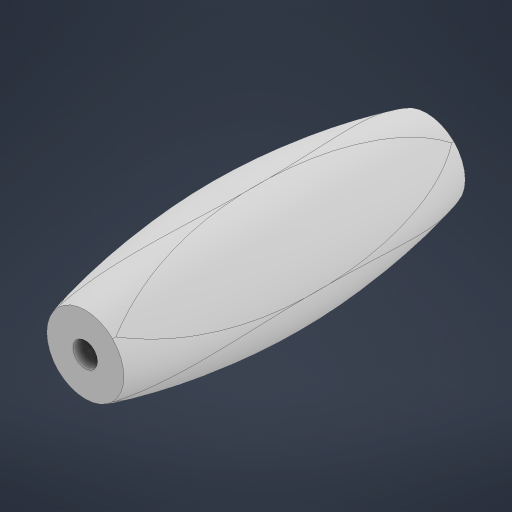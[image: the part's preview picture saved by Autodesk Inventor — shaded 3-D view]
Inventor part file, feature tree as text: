
AUTODESK INVENTOR PART (.ipt)
format: ipt  version: 2023 (Build 270158000, 158)  size: 424,448 bytes
history: native  units: mm
features: extrude x4, sketch x3, fillet x2
ambient origin geometry x8: Origin, YZ Plane, XZ Plane, XY Plane, X Axis, Y Axis, Z Axis, Center Point
bodies: Solid1 (feature_tree)
feature tree (9):
  extrude  "Extrusion1"  Depth=15.0mm
  sketch  "Sketch2"  dims[d2=3.0mm d3=41.999916mm d4=0.0mm]
  sketch  "Sketch3"  dims[d5=2.0mm d6=2.0mm d7=2.0mm d8=2.0mm d9=41.999916mm d10=0.0mm d11=41.999916mm d12=0.0mm d13=41.999916mm d14=0.0mm d15=7.49mm d16=5.0mm]
  extrude  "Extrusion2"  Depth=41.999916mm TaperAngle=0.0deg
  extrude  "Extrusion3"  Depth=2.0mm
  extrude  "Extrusion4"  Depth=2.0mm
  fillet  "Fillet1"  Radius=2.0mm
  fillet  "Fillet2"  Radius=41.999916mm
  sketch  "Sketch1"  dims[d0=15.0mm d1=15.0mm]
